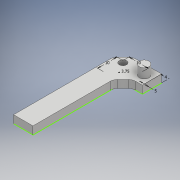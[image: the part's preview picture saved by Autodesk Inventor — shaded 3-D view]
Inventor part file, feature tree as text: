
AUTODESK INVENTOR PART (.ipt)
format: ipt  version: 2018.2 (Build 222227000, 227)  size: 126,976 bytes
history: native  units: mm
features: extrude x2, chamfer x2, fillet x2, sketch x1
ambient origin geometry x8: Origin, YZ Plane, XZ Plane, XY Plane, X Axis, Y Axis, Z Axis, Center Point
bodies: Solid1 (feature_tree)
feature tree (7):
  sketch  "Sketch1"  dims[d0=3.75mm d1=10.0mm d2=10.0mm d3=5.0mm d4=4.0mm d5=4.0mm d6=0.0mm d7=5.0mm d8=2.0mm d9=45.0deg d10=9.0mm d11=0.0mm d12=5.0mm d13=2.0mm d14=45.0deg d15=4.0mm d16=4.0mm]
  extrude  "Extrusion1"  Depth=10.0mm
  chamfer  "Chamfer1"  Distance=10.0mm
  extrude  "Extrusion2"  Depth=5.0mm
  chamfer  "Chamfer2"  Distance=4.0mm
  fillet  "Fillet1"  Radius=4.0mm
  fillet  "Fillet2"  Radius=5.0mm
